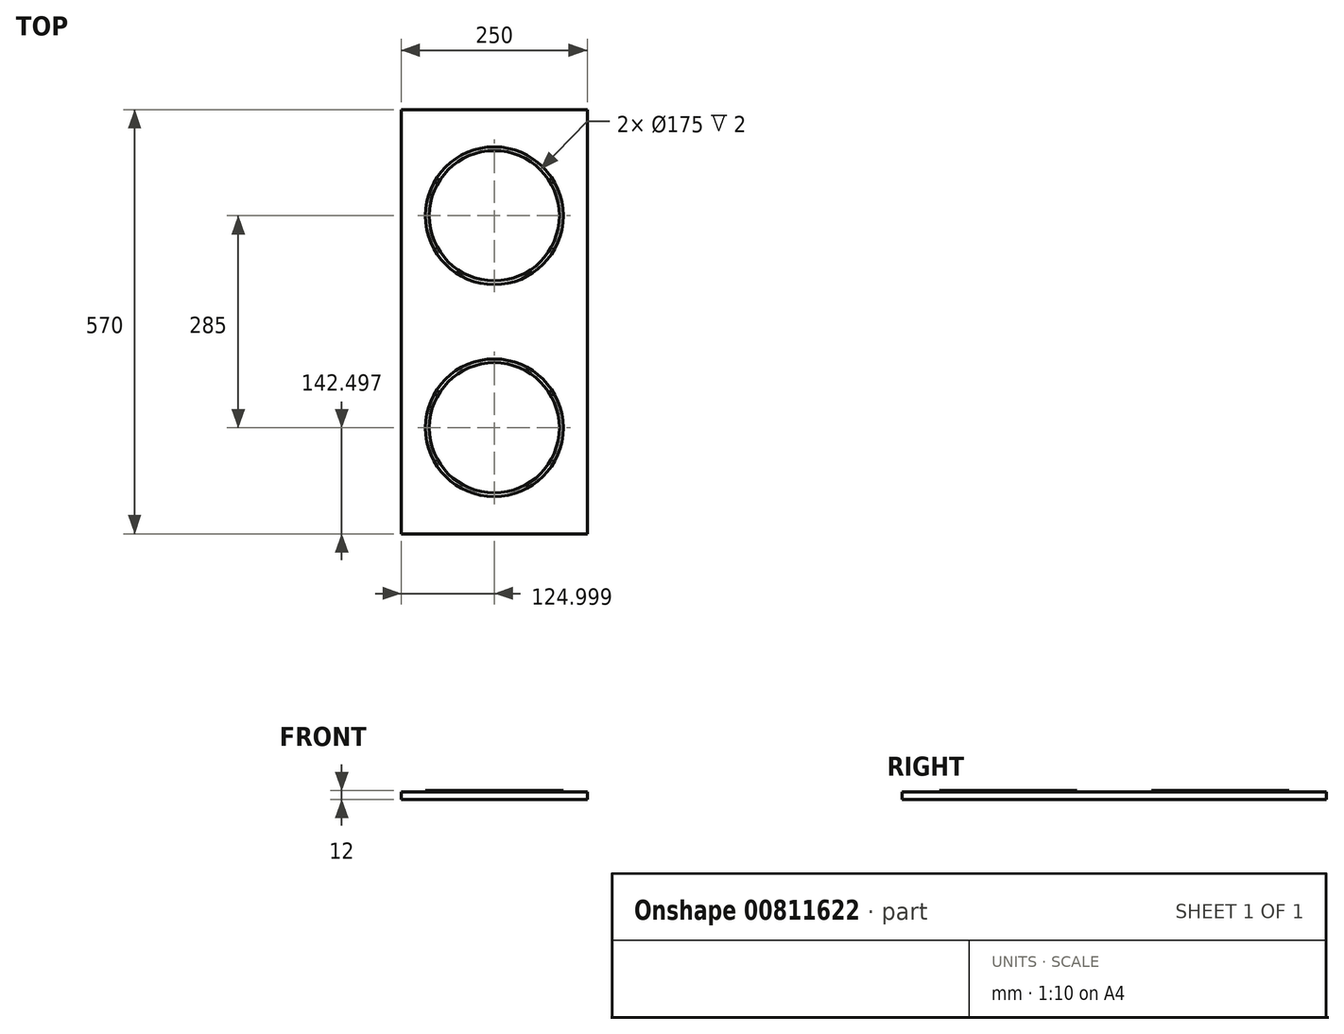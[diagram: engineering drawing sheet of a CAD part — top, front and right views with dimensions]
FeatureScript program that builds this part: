
annotation { "Feature Type Name" : "Feature", "Feature Type Description" : "" }
export const myFeature = defineFeature(function(context is Context, id is Id, definition is map)
    precondition{}
    {
        {
            var Q0;
            Q0=qCreatedBy(makeId("Top.planeOp"),FACE);
            var sketch = newSketch(context, id + "F0", { "sketchPlane" : qUnion([Q0])});
            skLineSegment(sketch, "E0.bottom", {"start": v(-11.84, 533) * mm, "end": v(238.16, 533) * mm});
            skLineSegment(sketch, "E0.top", {"start": v(-11.84, -37) * mm, "end": v(238.16, -37) * mm});
            skLineSegment(sketch, "E0.left", {"start": v(-11.84, 533) * mm, "end": v(-11.84, -37) * mm});
            skLineSegment(sketch, "E0.right", {"start": v(238.16, 533) * mm, "end": v(238.16, -37) * mm});
            skSolve(sketch);
        }
        {
            var Q0;
            Q0=qSketchRegion(id+"F0",true);
            extrude(context, id + "F1", {"entities" : qUnion([Q0]), "depth" : 10 * mm});
        }
        {
            var Q0;
            Q0=makeQuery(id+"F1.opExtrude","CAP_FACE",FACE,{"disambiguationData":[OSD([sQuery(id+"F0.wireOp",EDGE,"E0.bottom"),sQuery(id+"F0.wireOp",EDGE,"E0.top"),sQuery(id+"F0.wireOp",EDGE,"E0.left"),sQuery(id+"F0.wireOp",EDGE,"E0.right")])],"isStart":false});
            var sketch = newSketch(context, id + "F2", { "sketchPlane" : qUnion([Q0])});
            skLineSegment(sketch, "E1", {"start": v(238.16, 248) * mm, "end": v(-11.84, 248) * mm});
            skLineSegment(sketch, "E2", {"start": v(-11.84, 248) * mm, "end": v(238.16, 533) * mm});
            skLineSegment(sketch, "E3", {"start": v(238.16, 248) * mm, "end": v(-11.84, -37) * mm});
            skCircle(sketch, "E4", {"center": v(113.16, 390.5) * mm, "radius": 87.5 * mm});
            skCircle(sketch, "E5", {"center": v(113.16, 105.5) * mm, "radius": 87.5 * mm});
            skCircle(sketch, "E6.0", {"center": v(113.16, 390.5) * mm, "radius": 92.5 * mm});
            skCircle(sketch, "E7.0", {"center": v(113.16, 105.5) * mm, "radius": 92.5 * mm});
            skSolve(sketch);
        }
        {
            var Q0;
            Q0=qSketchRegion(id+"F2",true);
            extrude(context, id + "F3", {"entities" : qUnion([Q0]), "operationType" : NewBodyOperationType.ADD, "depth" : 2 * mm});
        }
    });
